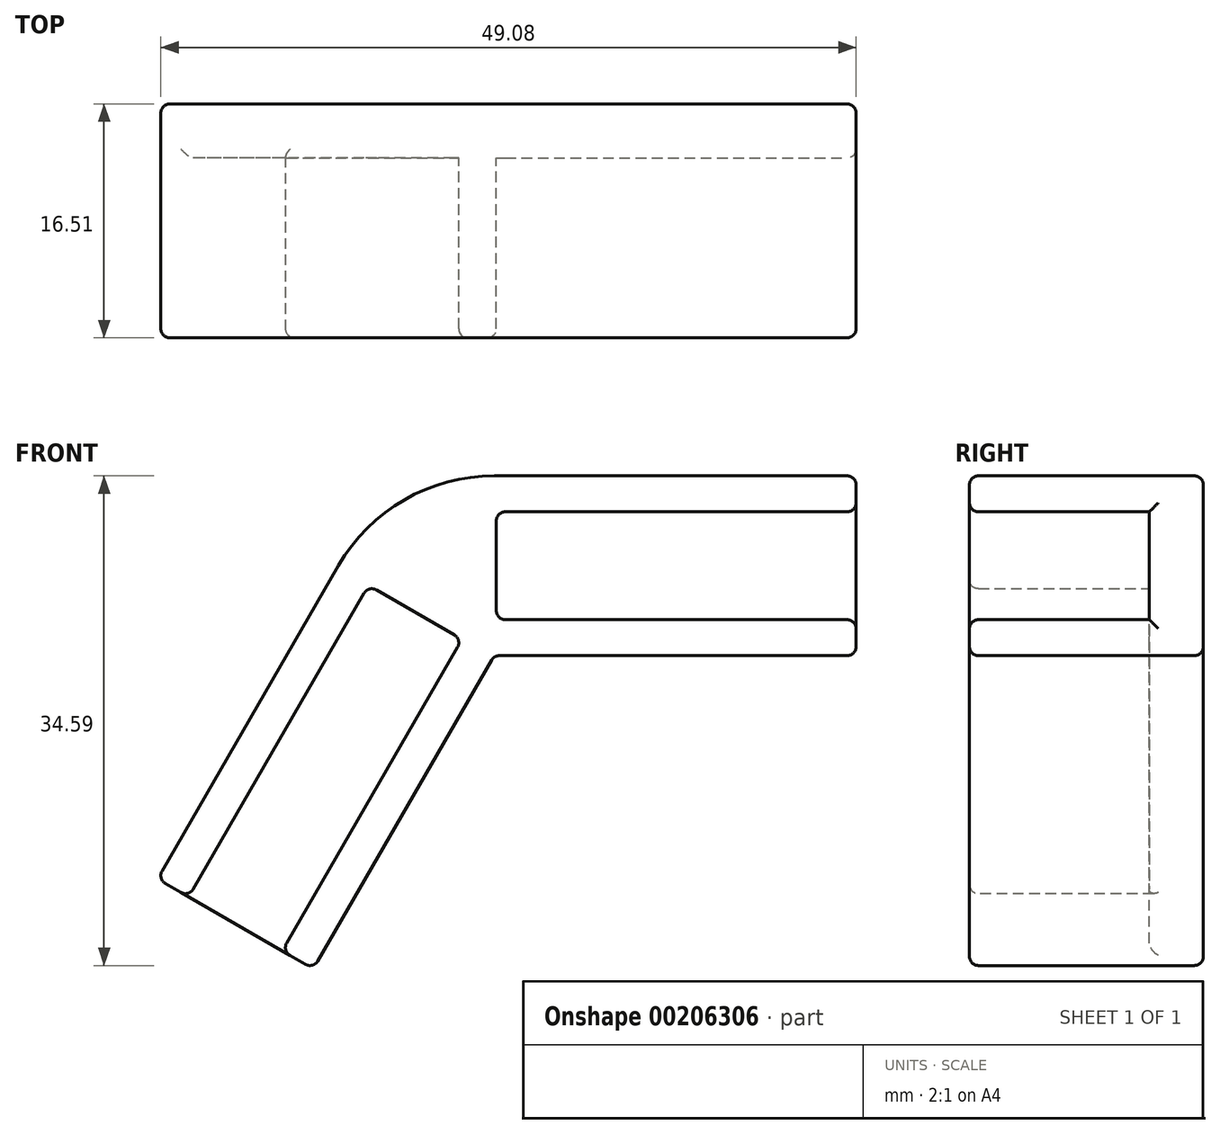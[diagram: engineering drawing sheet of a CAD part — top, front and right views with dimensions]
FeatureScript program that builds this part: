
annotation { "Feature Type Name" : "Feature", "Feature Type Description" : "" }
export const myFeature = defineFeature(function(context is Context, id is Id, definition is map)
    precondition{}
    {
        {
            var Q0;
            Q0=qCreatedBy(makeId("Front.planeOp"),FACE);
            var sketch = newSketch(context, id + "F0", { "sketchPlane" : qUnion([Q0])});
            skLineSegment(sketch, "E0.1", {"start": v(29.21, 3.81) * mm, "end": v(4.45, 3.81) * mm});
            skLineSegment(sketch, "E0.4", {"start": v(4.44, -3.81) * mm, "end": v(29.21, -3.8) * mm});
            skLineSegment(sketch, "E1", {"start": v(3.67, 6.35) * mm, "end": v(29.2, 6.35) * mm});
            skLineSegment(sketch, "E2", {"start": v(29.21, -6.35) * mm, "end": v(3.67, -6.35) * mm});
            skLineSegment(sketch, "E3", {"start": v(29.21, 3.81) * mm, "end": v(29.21, 6.35) * mm});
            skLineSegment(sketch, "E4", {"start": v(29.21, -6.35) * mm, "end": v(29.21, -3.8) * mm});
            skLineSegment(sketch, "E5", {"start": v(3.81, 3.18) * mm, "end": v(3.81, -3.18) * mm});
            skArc(sketch, "E6.filletArc", {"start": v(4.45, 3.81) * mm, "mid": v(4, 3.62) * mm, "end": v(3.81, 3.18) * mm});
            skArc(sketch, "E7.filletArc", {"start": v(3.8, -3.18) * mm, "mid": v(4, -3.62) * mm, "end": v(4.44, -3.81) * mm});
            skPoint(sketch, "E8", {"position": v(3.81, 0) * mm});
            skLineSegment(sketch, "E9.1.0", {"start": v(-5.52, -1.94) * mm, "end": v(-17.9, -23.4) * mm});
            skLineSegment(sketch, "E9.1.1", {"start": v(-11.3, -27.2) * mm, "end": v(1.08, -5.75) * mm});
            skLineSegment(sketch, "E9.1.2", {"start": v(-11.3, -27.2) * mm, "end": v(-9.1, -28.47) * mm});
            skLineSegment(sketch, "E9.1.3", {"start": v(0.84, -4.89) * mm, "end": v(-4.65, -1.71) * mm});
            skLineSegment(sketch, "E9.1.4", {"start": v(-20.1, -22.12) * mm, "end": v(-7.33, 0) * mm});
            skArc(sketch, "E9.1.5", {"start": v(1.08, -5.75) * mm, "mid": v(1.14, -5.27) * mm, "end": v(0.84, -4.89) * mm});
            skPoint(sketch, "E9.1.6", {"position": v(-1.9, -3.3) * mm});
            skLineSegment(sketch, "E9.1.7", {"start": v(-20.1, -22.12) * mm, "end": v(-17.9, -23.4) * mm});
            skLineSegment(sketch, "E9.1.8", {"start": v(3.67, -6.35) * mm, "end": v(-9.1, -28.47) * mm});
            skArc(sketch, "E9.1.9", {"start": v(-4.65, -1.71) * mm, "mid": v(-5.14, -1.65) * mm, "end": v(-5.52, -1.94) * mm});
            skPoint(sketch, "E9.center", {"position": v(0, 0) * mm});
            skLineSegment(sketch, "E9.anchor1", {"start": v(0, 0) * mm, "end": v(3.67, -6.35) * mm, "construction": true});
            skLineSegment(sketch, "E9.anchor2", {"start": v(0, 0) * mm, "end": v(-7.33, 0) * mm, "construction": true});
            skArc(sketch, "E10", {"start": v(3.67, 6.35) * mm, "mid": v(-2.68, 4.65) * mm, "end": v(-7.33, 0) * mm});
            skSolve(sketch);
        }
        {
            var Q0;
            Q0=makeQuery(id+"F0.imprint","IMPRINT",FACE,{"disambiguationData":[TD([[makeQuery(id+"F0.imprint","IMPRINT",EDGE,{"derivedFrom":sQuery(id+"F0.wireOp",EDGE,"E0.1")}),-1.0]])]});
            extrude(context, id + "F1", {"entities" : qUnion([Q0]), "depth" : 12.7 * mm});
        }
        {
            var Q0;
            Q0=makeQuery(id+"F1.opExtrude","CAP_FACE",FACE,{"disambiguationData":[OSD([sQuery(id+"F0.wireOp",EDGE,"E0.1"),sQuery(id+"F0.wireOp",EDGE,"E0.4"),sQuery(id+"F0.wireOp",EDGE,"E1"),sQuery(id+"F0.wireOp",EDGE,"E2"),sQuery(id+"F0.wireOp",EDGE,"E3"),sQuery(id+"F0.wireOp",EDGE,"E4"),sQuery(id+"F0.wireOp",EDGE,"E5"),sQuery(id+"F0.wireOp",EDGE,"E6.filletArc"),sQuery(id+"F0.wireOp",EDGE,"E7.filletArc"),sQuery(id+"F0.wireOp",EDGE,"E9.1.0"),sQuery(id+"F0.wireOp",EDGE,"E9.1.1"),sQuery(id+"F0.wireOp",EDGE,"E9.1.2"),sQuery(id+"F0.wireOp",EDGE,"E9.1.3"),sQuery(id+"F0.wireOp",EDGE,"E9.1.4"),sQuery(id+"F0.wireOp",EDGE,"E9.1.5"),sQuery(id+"F0.wireOp",EDGE,"E9.1.7"),sQuery(id+"F0.wireOp",EDGE,"E9.1.8"),sQuery(id+"F0.wireOp",EDGE,"E9.1.9"),sQuery(id+"F0.wireOp",EDGE,"E10")])],"isStart":true});
            var sketch = newSketch(context, id + "F2", { "sketchPlane" : qUnion([Q0])});
            skLineSegment(sketch, "E11", {"start": v(-29.21, 6.35) * mm, "end": v(-29.21, -6.35) * mm});
            skLineSegment(sketch, "E12", {"start": v(-29.21, -6.35) * mm, "end": v(-3.67, -6.35) * mm});
            skLineSegment(sketch, "E13", {"start": v(-3.67, -6.35) * mm, "end": v(9.1, -28.47) * mm});
            skLineSegment(sketch, "E14", {"start": v(9.1, -28.47) * mm, "end": v(11.3, -27.2) * mm});
            skLineSegment(sketch, "E15", {"start": v(11.3, -27.2) * mm, "end": v(20.1, -22.12) * mm});
            skLineSegment(sketch, "E16", {"start": v(20.1, -22.12) * mm, "end": v(7.33, 0) * mm});
            skLineSegment(sketch, "E17", {"start": v(-3.67, 6.35) * mm, "end": v(-29.21, 6.35) * mm});
            skArc(sketch, "E18", {"start": v(7.33, 0) * mm, "mid": v(2.68, 4.65) * mm, "end": v(-3.67, 6.35) * mm});
            skSolve(sketch);
        }
        {
            var Q0;
            Q0 = qSketchRegion(id + "F2", true);
            extrude(context, id + "F3", {"entities" : qUnion([Q0]), "operationType" : NewBodyOperationType.ADD, "depth" : 3.8 * mm});
        }
        {
            var Q0;
            Q0=makeQuery(id+"F1.opExtrude","CAP_FACE",FACE,{"disambiguationData":[OSD([sQuery(id+"F0.wireOp",EDGE,"E0.1"),sQuery(id+"F0.wireOp",EDGE,"E0.4"),sQuery(id+"F0.wireOp",EDGE,"E1"),sQuery(id+"F0.wireOp",EDGE,"E2"),sQuery(id+"F0.wireOp",EDGE,"E3"),sQuery(id+"F0.wireOp",EDGE,"E4"),sQuery(id+"F0.wireOp",EDGE,"E5"),sQuery(id+"F0.wireOp",EDGE,"E6.filletArc"),sQuery(id+"F0.wireOp",EDGE,"E7.filletArc"),sQuery(id+"F0.wireOp",EDGE,"E9.1.0"),sQuery(id+"F0.wireOp",EDGE,"E9.1.1"),sQuery(id+"F0.wireOp",EDGE,"E9.1.2"),sQuery(id+"F0.wireOp",EDGE,"E9.1.3"),sQuery(id+"F0.wireOp",EDGE,"E9.1.4"),sQuery(id+"F0.wireOp",EDGE,"E9.1.5"),sQuery(id+"F0.wireOp",EDGE,"E9.1.7"),sQuery(id+"F0.wireOp",EDGE,"E9.1.8"),sQuery(id+"F0.wireOp",EDGE,"E9.1.9"),sQuery(id+"F0.wireOp",EDGE,"E10")])],"isStart":false});
            var Q1;
            Q1=makeQuery(id+"F3.boolean.opBoolean","MERGE",FACE,{"derivedFrom":[makeQuery(id+"F1.opExtrude","SWEPT_FACE",FACE,{"disambiguationData":[OSD([sQuery(id+"F0.wireOp",EDGE,"E3")])]}),makeQuery(id+"F1.opExtrude","SWEPT_FACE",FACE,{"disambiguationData":[OSD([sQuery(id+"F0.wireOp",EDGE,"E4")])]}),makeQuery(id+"F3.opExtrude","SWEPT_FACE",FACE,{"disambiguationData":[OSD([sQuery(id+"F2.wireOp",EDGE,"E11")])]})]});
            var Q2;
            Q2=makeQuery(id+"F3.boolean.opBoolean","MERGE",FACE,{"derivedFrom":[makeQuery(id+"F1.opExtrude","SWEPT_FACE",FACE,{"disambiguationData":[OSD([sQuery(id+"F0.wireOp",EDGE,"E9.1.2")])]}),makeQuery(id+"F1.opExtrude","SWEPT_FACE",FACE,{"disambiguationData":[OSD([sQuery(id+"F0.wireOp",EDGE,"E9.1.7")])]}),makeQuery(id+"F3.opExtrude","SWEPT_FACE",FACE,{"disambiguationData":[OSD([sQuery(id+"F2.wireOp",EDGE,"E14"),sQuery(id+"F2.wireOp",EDGE,"E15")])]})]});
            var Q3;
            Q3=makeQuery(id+"F3.opExtrude","CAP_FACE",FACE,{"disambiguationData":[OSD([sQuery(id+"F2.wireOp",EDGE,"E11"),sQuery(id+"F2.wireOp",EDGE,"E12"),sQuery(id+"F2.wireOp",EDGE,"E13"),sQuery(id+"F2.wireOp",EDGE,"E14"),sQuery(id+"F2.wireOp",EDGE,"E15"),sQuery(id+"F2.wireOp",EDGE,"E16"),sQuery(id+"F2.wireOp",EDGE,"E17"),sQuery(id+"F2.wireOp",EDGE,"E18")])],"isStart":false});
            var Q4;
            Q4=makeQuery(id+"F3.boolean.opBoolean","MERGE",FACE,{"derivedFrom":[makeQuery(id+"F1.opExtrude","SWEPT_FACE",FACE,{"disambiguationData":[OSD([sQuery(id+"F0.wireOp",EDGE,"E9.1.8")])]}),makeQuery(id+"F3.opExtrude","SWEPT_FACE",FACE,{"disambiguationData":[OSD([sQuery(id+"F2.wireOp",EDGE,"E13")])]})]});
            fillet(context, id + "F4", {"entities" : qUnion([Q0, Q1, Q2, Q3, Q4]), "radius" : 0.64 * mm, "tangentPropagation" : true, "allowEdgeOverflow" : false});
        }
    });
